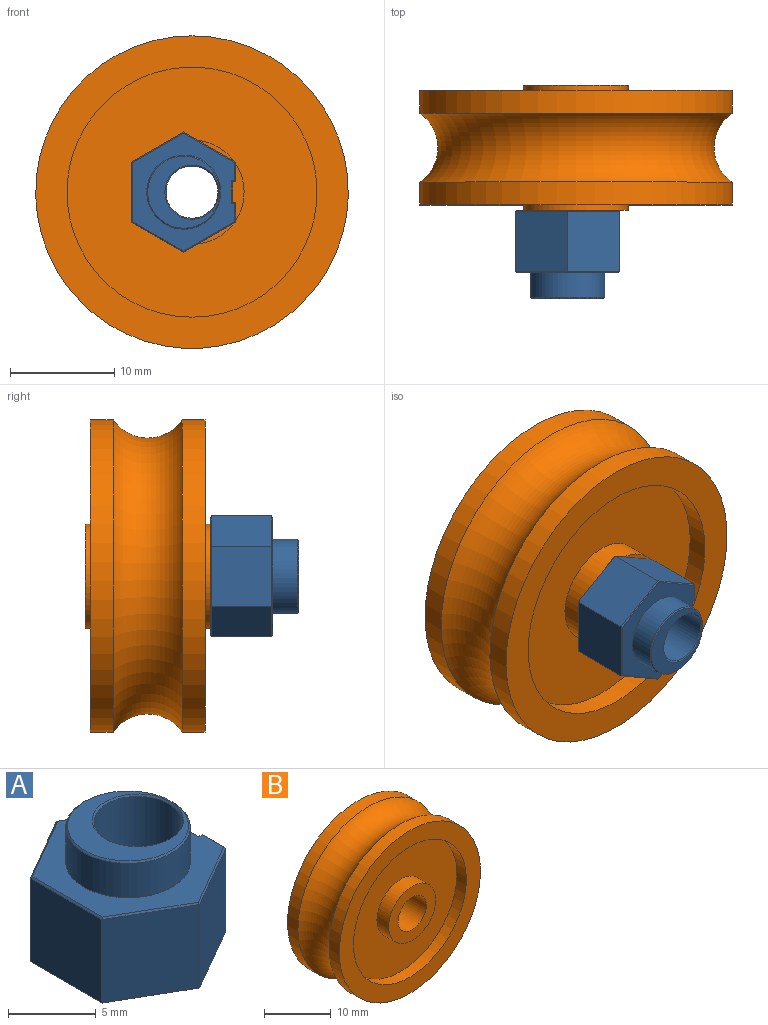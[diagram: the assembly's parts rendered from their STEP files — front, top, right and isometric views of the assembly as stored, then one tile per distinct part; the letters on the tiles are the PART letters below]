
ASSEMBLY  parts=2 mates=1
PART A: 38 faces, bbox 10x11.5x8.5 mm
  f0: plane 5.8x1.89mm, normal (1,0,0), area 10.9mm2, adj f7,f12,f22,f31
  f1: plane 11.32x9.8mm, normal (0,0,1), area 42.8mm2, adj f10,f28,f29,f30,f31,f32,f33,f34
  f2: plane 11.32x9.8mm, normal (0,0,-1), area 61.3mm2, adj f15,f16,f17,f18,f19,f20,f21,f22
  f3: plane 5.8x5mm, normal (0.5,0.87,0), area 33.5mm2, adj f4,f8,f17,f34
  f4: plane 5.8x5mm, normal (-0.5,0.87,0), area 33.5mm2, adj f3,f5,f15,f36
  f5: plane 5.8x5.77mm, normal (-1,0,0), area 33.5mm2, adj f4,f6,f16,f37
  f6: plane 5.8x5mm, normal (-0.5,-0.87,0), area 33.5mm2, adj f5,f7,f18,f35
  f7: plane 5.8x5mm, normal (0.5,-0.87,0), area 33.5mm2, adj f0,f6,f20,f33
  f8: plane 5.8x1.89mm, normal (1,0,0), area 10.9mm2, adj f3,f13,f19,f32
  f9: cylinder r=2.5mm len=8.3mm, axis (0,0,-1), area 130.4mm2, adj f25,f26
  f10: cylinder r=3.56mm len=7.11mm, axis (0,0,-1), area 53.6mm2, adj f1,f27
  f11: plane 6.91x6.91mm, normal (0,0,1), area 16.3mm2, adj f26,f27
  f12: plane 5.8x0.3mm, normal (0,1,0), area 1.7mm2, adj f0,f14,f24,f29
  f13: plane 5.8x0.3mm, normal (0,-1,0), area 1.7mm2, adj f8,f14,f21,f30
  f14: plane 5.8x2mm, normal (1,0,0), area 11.6mm2, adj f12,f13,f23,f28
  f15: plane 5x2.94mm, normal (-0.35,0.61,-0.71), area 0.8mm2, adj f2,f4,f16,f17
  f16: plane 5.77x0.1mm, normal (-0.71,0,-0.71), area 0.8mm2, adj f2,f5,f15,f18
  f17: plane 5x2.94mm, normal (0.35,0.61,-0.71), area 0.8mm2, adj f2,f3,f15,f19
  f18: plane 5x2.94mm, normal (-0.35,-0.61,-0.71), area 0.8mm2, adj f2,f6,f16,f20
  f19: plane 1.89x0.1mm, normal (0.71,0,-0.71), area 0.3mm2, adj f2,f8,f17,f21
  f20: plane 5x2.94mm, normal (0.35,-0.61,-0.71), area 0.8mm2, adj f2,f7,f18,f22
  f21: plane 0.4x0.1mm, normal (0,-0.71,-0.71), area 0mm2, adj f2,f13,f19,f23
  f22: plane 1.89x0.1mm, normal (0.71,0,-0.71), area 0.3mm2, adj f0,f2,f20,f24
  f23: plane 2.2x0.1mm, normal (0.71,0,-0.71), area 0.3mm2, adj f2,f14,f21,f24
  f24: plane 0.4x0.1mm, normal (0,0.71,-0.71), area 0mm2, adj f2,f12,f22,f23
  f25: cone r=2.6mm half-angle=45deg, axis (0,0,-1), area 2.3mm2, adj f2,f9
  f26: cone r=2.5mm half-angle=45deg, axis (0,0,1), area 2.3mm2, adj f9,f11
  f27: cone r=3.46mm half-angle=45deg, axis (0,0,-1), area 3.1mm2, adj f10,f11
  f28: plane 2.2x0.1mm, normal (0.71,0,0.71), area 0.3mm2, adj f1,f14,f29,f30
  f29: plane 0.4x0.1mm, normal (0,0.71,0.71), area 0mm2, adj f1,f12,f28,f31
  f30: plane 0.4x0.1mm, normal (0,-0.71,0.71), area 0mm2, adj f1,f13,f28,f32
  f31: plane 1.89x0.1mm, normal (0.71,0,0.71), area 0.3mm2, adj f0,f1,f29,f33
  f32: plane 1.89x0.1mm, normal (0.71,0,0.71), area 0.3mm2, adj f1,f8,f30,f34
  f33: plane 5x2.94mm, normal (0.35,-0.61,0.71), area 0.8mm2, adj f1,f7,f31,f35
  f34: plane 5x2.94mm, normal (0.35,0.61,0.71), area 0.8mm2, adj f1,f3,f32,f36
  f35: plane 5x2.94mm, normal (-0.35,-0.61,0.71), area 0.8mm2, adj f1,f6,f33,f37
  f36: plane 5x2.94mm, normal (-0.35,0.61,0.71), area 0.8mm2, adj f1,f4,f34,f37
  f37: plane 5.77x0.1mm, normal (-0.71,0,0.71), area 0.8mm2, adj f1,f5,f35,f36
PART B: 14 faces, bbox 37.3x12x37.3 mm
  f0: torus R=17.25mm, axis (0,1,0), area 677.8mm2, adj f1,f8
  f1: cylinder r=15mm len=30mm, axis (0,1,0), area 206.7mm2, adj f0,f2
  f2: plane 30x30mm, normal (0,-1,0), area 254.5mm2, adj f1,f3
  f3: cylinder r=12mm len=24mm, axis (0,-1,0), area 150.8mm2, adj f2,f4
  f4: plane 24x24mm, normal (0,-1,0), area 373.8mm2, adj f3,f7
  f5: cylinder r=3mm len=12mm, axis (0,1,0), area 226.2mm2, adj f6,f12
  f6: plane 10x10mm, normal (0,-1,0), area 50.3mm2, adj f5,f7
  f7: cylinder r=5mm len=10mm, axis (0,1,0), area 78.5mm2, adj f4,f6
  f8: cylinder r=15mm len=30mm, axis (0,-1,0), area 206.7mm2, adj f0,f9
  f9: plane 30x30mm, normal (0,1,0), area 254.5mm2, adj f8,f10
  f10: cylinder r=12mm len=24mm, axis (0,1,0), area 150.8mm2, adj f9,f11
  f11: plane 24x24mm, normal (0,1,0), area 373.8mm2, adj f10,f13
  f12: plane 10x10mm, normal (0,1,0), area 50.3mm2, adj f5,f13
  f13: cylinder r=5mm len=10mm, axis (0,-1,0), area 78.5mm2, adj f11,f12
PLACE A rot(axis=(1,0,0),90deg) t=(-0.79,-6,0)mm
PLACE B at identity
MATE fastened A.f9 <-> B.f5  axis (0,1,0) through (0,-6,0)mm
